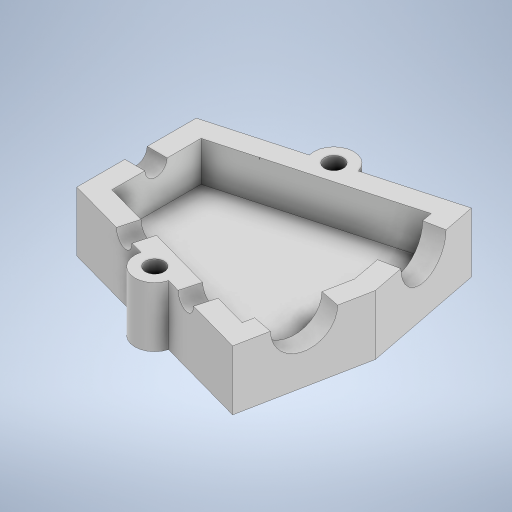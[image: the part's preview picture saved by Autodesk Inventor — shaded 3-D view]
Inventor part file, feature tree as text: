
AUTODESK INVENTOR PART (.ipt)
format: ipt  version: 2024 (Build 280153000, 153)  size: 361,984 bytes
history: native  units: in
note: dims shown in document units (in); Inventor stores cm internally (conversion verified against a paired STEP export)
features: extrude x8, sketch x8, mirror x1, projected_geometry x1
ambient origin geometry x8: Origin, YZ Plane, XZ Plane, XY Plane, X Axis, Y Axis, Z Axis, Center Point
bodies: Solid1 (feature_tree)
feature tree (18):
  extrude  "Extrusion1"  Depth=0.75in
  extrude  "Extrusion3"  Depth=0.75in
  extrude  "Extrusion4"  Depth=0.125in
  extrude  "Extrusion5"  Depth=0.375in TaperAngle=0.0deg
  extrude  "Extrusion6"  Depth=1.0in TaperAngle=0.0deg
  extrude  "Extrusion7"  Depth=1.0in TaperAngle=0.0deg
  extrude  "Extrusion8"  Depth=0.375in TaperAngle=0.0deg
  extrude  "Extrusion9"  Depth=0.375in TaperAngle=0.0deg
  mirror  "Mirror1"
  sketch  "Sketch1"  dims[d0=1.0in d1=0.75in]
  sketch  "Sketch3"  dims[d2=0.5in d3=0.75in]
  sketch  "Sketch4"  dims[d4=0.125in d5=0.125in]
  sketch  "Sketch5"  dims[d6=0.125in d7=0.375in d8=0.0in]
  sketch  "Sketch6"  dims[d12=0.36in d13=1.0in d14=0.0in]
  projected_geometry  "Projected Loop1"
  sketch  "Sketch7"  dims[d15=0.36in d16=1.0in d17=0.0in]
  sketch  "Sketch8"  dims[d18=0.14in d19=0.375in d20=0.0in]
  sketch  "Sketch10"  dims[d21=0.125in d22=0.0in d23=0.375in d24=0.0in d25=0.1181in d26=0.1181in d27=0.375in d28=0.0in d29=0.14in d30=0.14in d31=0.15in d32=0.15in d33=0.375in d34=0.0in]
